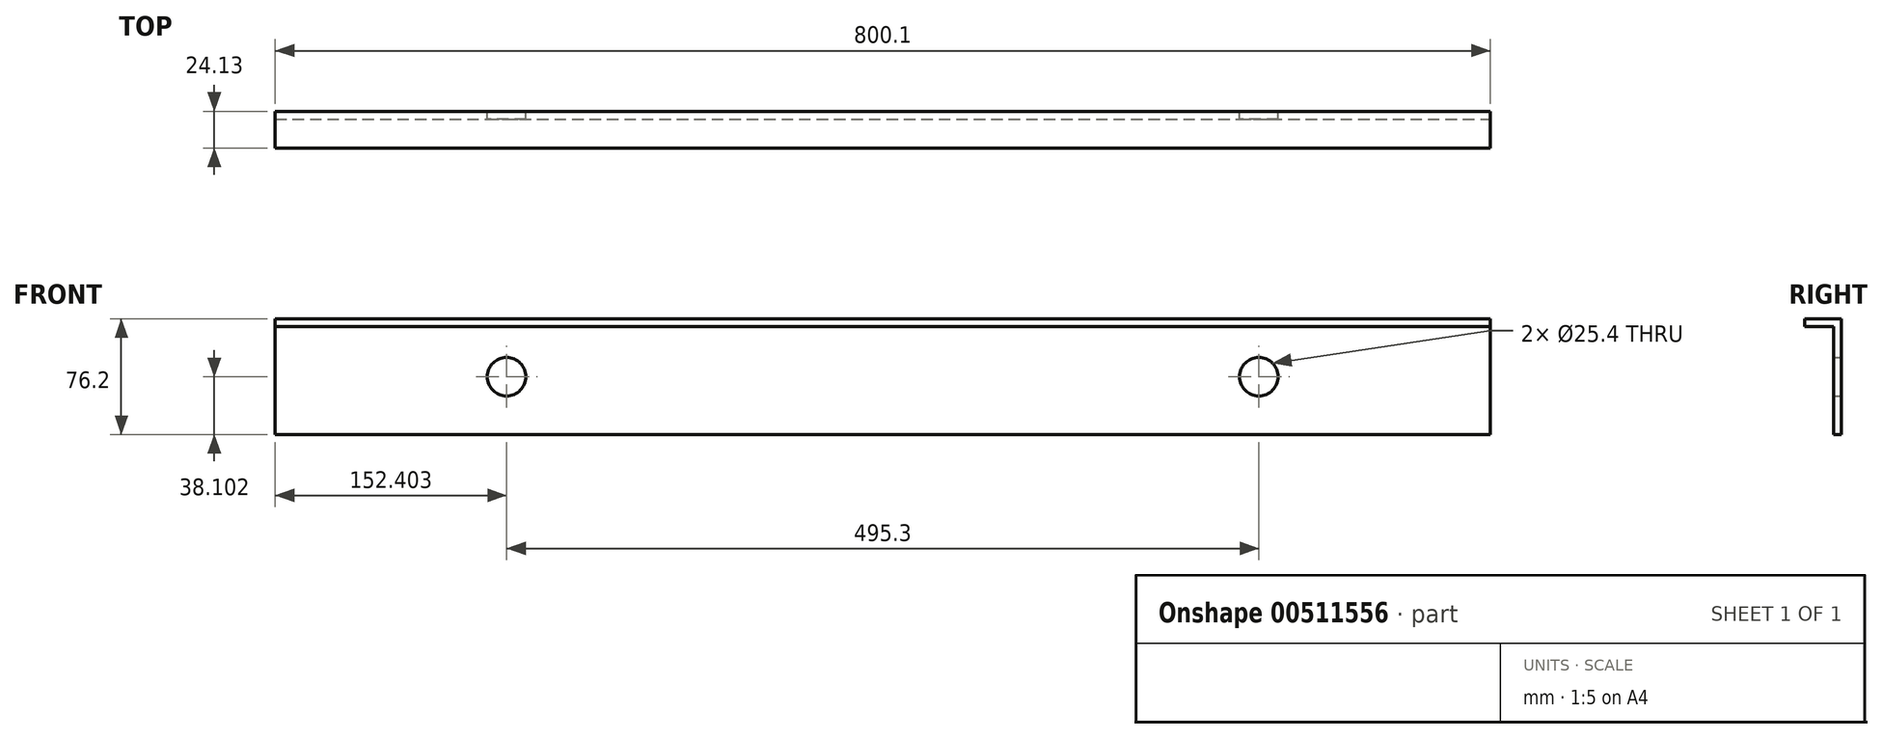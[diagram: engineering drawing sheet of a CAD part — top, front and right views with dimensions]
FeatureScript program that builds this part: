
annotation { "Feature Type Name" : "Feature", "Feature Type Description" : "" }
export const myFeature = defineFeature(function(context is Context, id is Id, definition is map)
    precondition{}
    {
        {
            var Q0;
            Q0=qCreatedBy(makeId("Front.planeOp"),FACE);
            var sketch = newSketch(context, id + "F0", { "sketchPlane" : qUnion([Q0])});
            skLineSegment(sketch, "E0.bottom", {"start": v(-392.3, -1.28) * mm, "end": v(407.8, -1.28) * mm});
            skLineSegment(sketch, "E0.top", {"start": v(-392.3, -77.48) * mm, "end": v(407.8, -77.48) * mm});
            skLineSegment(sketch, "E0.left", {"start": v(-392.3, -1.28) * mm, "end": v(-392.3, -77.48) * mm});
            skLineSegment(sketch, "E0.right", {"start": v(407.8, -1.28) * mm, "end": v(407.8, -77.48) * mm});
            skCircle(sketch, "E1", {"center": v(-239.9, -39.38) * mm, "radius": 12.7 * mm});
            skCircle(sketch, "E2", {"center": v(255.4, -39.38) * mm, "radius": 12.7 * mm});
            skSolve(sketch);
        }
        {
            var Q0;
            Q0=makeQuery(id+"F0.imprint","IMPRINT",FACE,{"disambiguationData":[TD([[makeQuery(id+"F0.imprint","IMPRINT",EDGE,{"derivedFrom":sQuery(id+"F0.wireOp",EDGE,"E0.bottom")}),-1.0]])]});
            extrude(context, id + "F1", {"entities" : qUnion([Q0]), "depth" : 5.08 * mm});
        }
        {
            var Q0;
            Q0=makeQuery(id+"F1.opExtrude","CAP_FACE",FACE,{"disambiguationData":[OSD([sQuery(id+"F0.wireOp",EDGE,"E0.bottom"),sQuery(id+"F0.wireOp",EDGE,"E0.top"),sQuery(id+"F0.wireOp",EDGE,"E0.left"),sQuery(id+"F0.wireOp",EDGE,"E0.right"),sQuery(id+"F0.wireOp",EDGE,"E1"),sQuery(id+"F0.wireOp",EDGE,"E2")])],"isStart":false});
            var sketch = newSketch(context, id + "F2", { "sketchPlane" : qUnion([Q0])});
            skLineSegment(sketch, "E3.bottom", {"start": v(-392.3, -1.28) * mm, "end": v(407.8, -1.28) * mm});
            skLineSegment(sketch, "E3.top", {"start": v(-392.3, -6.36) * mm, "end": v(407.8, -6.36) * mm});
            skLineSegment(sketch, "E3.left", {"start": v(-392.3, -1.28) * mm, "end": v(-392.3, -6.36) * mm});
            skLineSegment(sketch, "E3.right", {"start": v(407.8, -1.28) * mm, "end": v(407.8, -6.36) * mm});
            skSolve(sketch);
        }
        {
            var Q0;
            Q0 = qSketchRegion(id + "F2", true);
            extrude(context, id + "F3", {"entities" : qUnion([Q0]), "operationType" : NewBodyOperationType.ADD, "depth" : 19.05 * mm});
        }
    });
